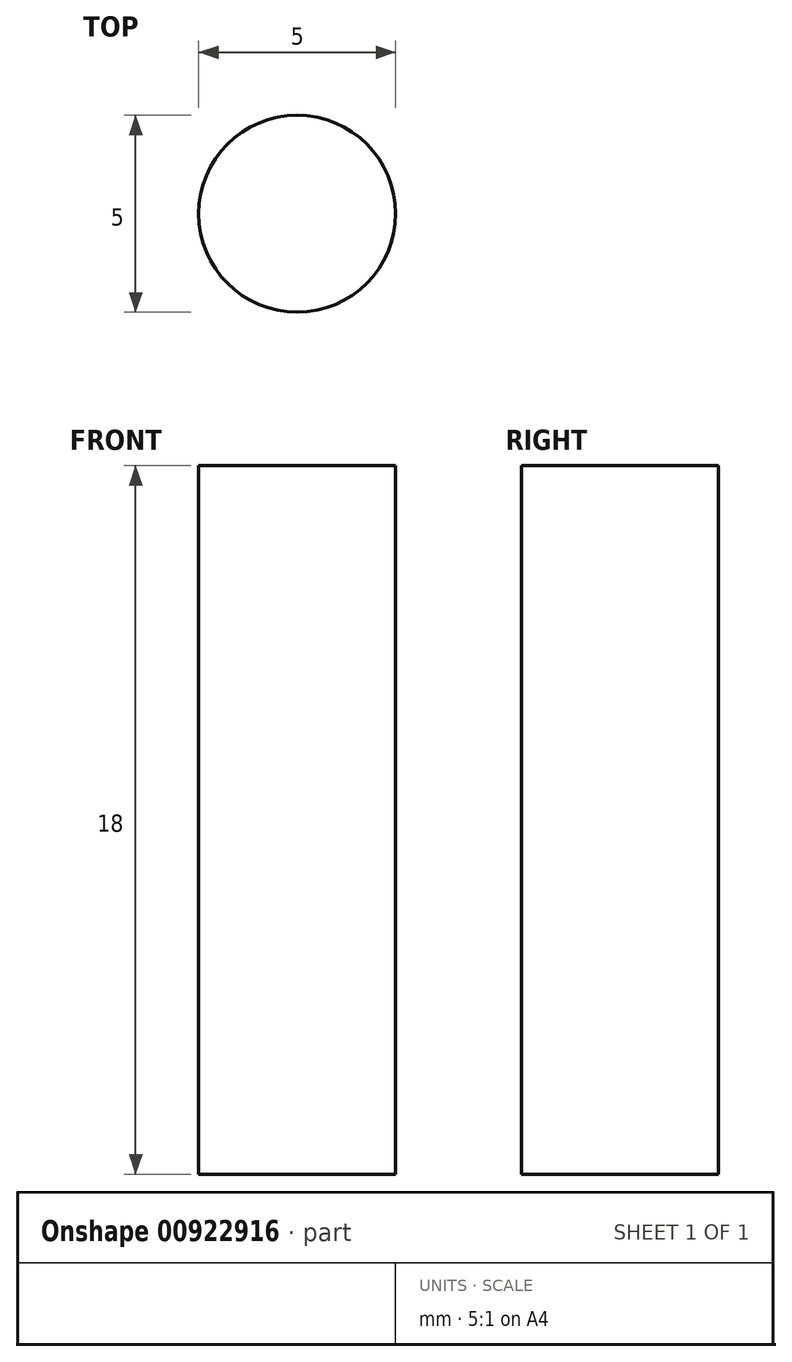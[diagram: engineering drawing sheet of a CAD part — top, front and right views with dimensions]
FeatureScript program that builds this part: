
annotation { "Feature Type Name" : "Feature", "Feature Type Description" : "" }
export const myFeature = defineFeature(function(context is Context, id is Id, definition is map)
    precondition{}
    {
        {
            var Q0;
            Q0=qCreatedBy(makeId("Front.planeOp"),FACE);
            var sketch = newSketch(context, id + "F0", { "sketchPlane" : qUnion([Q0])});
            skCircle(sketch, "E0", {"center": v(0, 0) * mm, "radius": 10 * mm});
            skLineSegment(sketch, "E1.right", {"start": v(-25, -2.5) * mm, "end": v(-25, 2.5) * mm});
            skLineSegment(sketch, "E2", {"start": v(-10, 0) * mm, "end": v(-10, -2.5) * mm});
            skLineSegment(sketch, "E3", {"start": v(-10, 0) * mm, "end": v(-10, 2.5) * mm});
            skLineSegment(sketch, "E4.trimOffspring", {"start": v(-10, 2.5) * mm, "end": v(-25, 2.5) * mm});
            skLineSegment(sketch, "E5.trimOffspring", {"start": v(-10, -2.5) * mm, "end": v(-25, -2.5) * mm});
            skPoint(sketch, "E1.left.start.orphan", {"position": v(25, -2.5) * mm});
            skPoint(sketch, "E1.top.start.orphan", {"position": v(25, 2.5) * mm});
            skLineSegment(sketch, "E6", {"start": v(0, 17.91) * mm, "end": v(0, -21.07) * mm, "construction": true});
            skLineSegment(sketch, "E7.MirrorCS", {"start": v(10, -2.5) * mm, "end": v(25, -2.5) * mm});
            skLineSegment(sketch, "E8.MirrorCS", {"start": v(25, -2.5) * mm, "end": v(25, 2.5) * mm});
            skLineSegment(sketch, "E9.MirrorCS", {"start": v(10, 2.5) * mm, "end": v(25, 2.5) * mm});
            skLineSegment(sketch, "E10.MirrorCS", {"start": v(10, 0) * mm, "end": v(10, 2.5) * mm});
            skLineSegment(sketch, "E11.MirrorCS", {"start": v(10, 0) * mm, "end": v(10, -2.5) * mm});
            skArc(sketch, "E12.0", {"start": v(11.62, 3) * mm, "mid": v(0, 12) * mm, "end": v(-11.62, 3) * mm});
            skLineSegment(sketch, "E13.0", {"start": v(11.62, 3) * mm, "end": v(25, 3) * mm});
            skLineSegment(sketch, "E14.MirrorCS", {"start": v(-11.62, 3) * mm, "end": v(-25, 3) * mm});
            skPoint(sketch, "E15.orphan", {"position": v(-10, 3) * mm});
            skPoint(sketch, "E16.orphan", {"position": v(10, 3) * mm});
            skLineSegment(sketch, "E17", {"start": v(-25, 3) * mm, "end": v(-25, 21) * mm});
            skLineSegment(sketch, "E18", {"start": v(-25, 21) * mm, "end": v(25, 21) * mm});
            skLineSegment(sketch, "E19", {"start": v(25, 21) * mm, "end": v(25, 3) * mm});
            skSolve(sketch);
        }
        {
            var Q0;
            Q0=makeQuery(id+"F0.imprint","IMPRINT",FACE,{"disambiguationData":[TD([[makeQuery(id+"F0.imprint","IMPRINT",EDGE,{"derivedFrom":sQuery(id+"F0.wireOp",EDGE,"E12.0")}),-1.0]])]});
            extrude(context, id + "F1", {"entities" : qUnion([Q0]), "surfaceOperationType" : NewSurfaceOperationType.ADD, "depth" : 17 * mm, "offsetDistance" : 25 * mm});
        }
        {
            var Q0;
            Q0=makeQuery(id+"F1.opExtrude","SWEPT_FACE",FACE,{"disambiguationData":[OSD([sQuery(id+"F0.wireOp",EDGE,"E18")])]});
            var sketch = newSketch(context, id + "F2", { "sketchPlane" : qUnion([Q0])});
            skLineSegment(sketch, "E20", {"start": v(-25, -8.5) * mm, "end": v(40.9, -8.5) * mm, "construction": true});
            skCircle(sketch, "E21", {"center": v(-17.5, -8.5) * mm, "radius": 2.5 * mm});
            skLineSegment(sketch, "E22", {"start": v(0, 0) * mm, "end": v(0, -17) * mm, "construction": true});
            skCircle(sketch, "E23.MirrorC", {"center": v(17.5, -8.5) * mm, "radius": 2.5 * mm});
            skSolve(sketch);
        }
        {
            var Q0;
            Q0=makeQuery(id+"F2.imprint","IMPRINT",FACE,{"disambiguationData":[TD([[makeQuery(id+"F2.imprint","IMPRINT",EDGE,{"derivedFrom":sQuery(id+"F2.wireOp",EDGE,"E21")}),1.0]])]});
            var Q1;
            Q1=makeQuery(id+"F2.imprint","IMPRINT",FACE,{"disambiguationData":[TD([[makeQuery(id+"F2.imprint","IMPRINT",EDGE,{"derivedFrom":sQuery(id+"F2.wireOp",EDGE,"E23.MirrorC")}),-1.0]])]});
            extrude(context, id + "F3", {"entities" : qUnion([Q0, Q1]), "operationType" : NewBodyOperationType.REMOVE, "oppositeDirection" : true, "depth" : 44.3 * mm, "offsetDistance" : 25 * mm});
        }
    });
